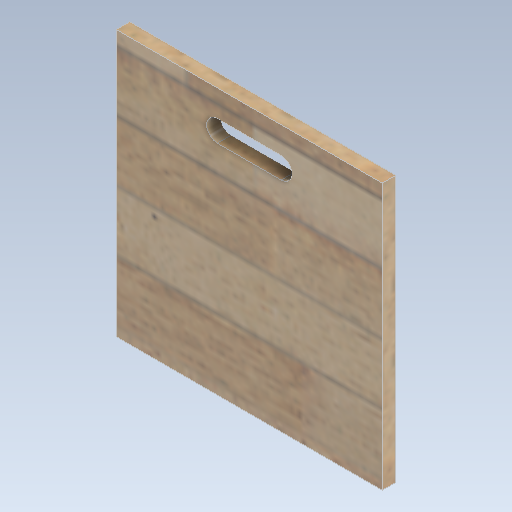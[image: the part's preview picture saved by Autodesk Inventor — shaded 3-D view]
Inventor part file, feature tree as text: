
AUTODESK INVENTOR PART (.ipt)
format: ipt  version: 2021 (Build 250183000, 183)  size: 243,712 bytes
history: native  units: mm
features: extrude x2, sketch x2
ambient origin geometry x8: Origin, YZ Plane, XZ Plane, XY Plane, X Axis, Y Axis, Z Axis, Center Point
bodies: Solid1 (feature_tree)
feature tree (4):
  extrude  "Extrusion1"  Depth=30.0mm
  extrude  "Extrusion2"  Depth=25.0mm
  sketch  "Sketch1"  dims[d3=0.0mm d4=30.0mm]
  sketch  "Sketch2"  dims[d5=20.0mm d6=25.0mm d7=12.7mm d8=0.0mm]
